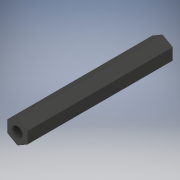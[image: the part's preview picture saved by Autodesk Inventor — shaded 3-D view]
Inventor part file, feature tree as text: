
AUTODESK INVENTOR PART (.ipt)
format: ipt  version: 2018 (Build 220112000, 112)  size: 103,936 bytes
history: native  units: in
note: dims shown in document units (in); Inventor stores cm internally (conversion verified against a paired STEP export)
features: extrude x1, sketch x1, other x1
ambient origin geometry x8: Origin, YZ Plane, XZ Plane, XY Plane, X Axis, Y Axis, Z Axis, Center Point
bodies: Solid1 (feature_tree)
feature tree (3):
  extrude  "Extrusion1"  Depth=4.3937in TaperAngle=0.0deg
  sketch  "Sketch1"  dims[d0=0.25in d1=4.3937in d2=0.0in]
  other  "Boss-Extrude1"
